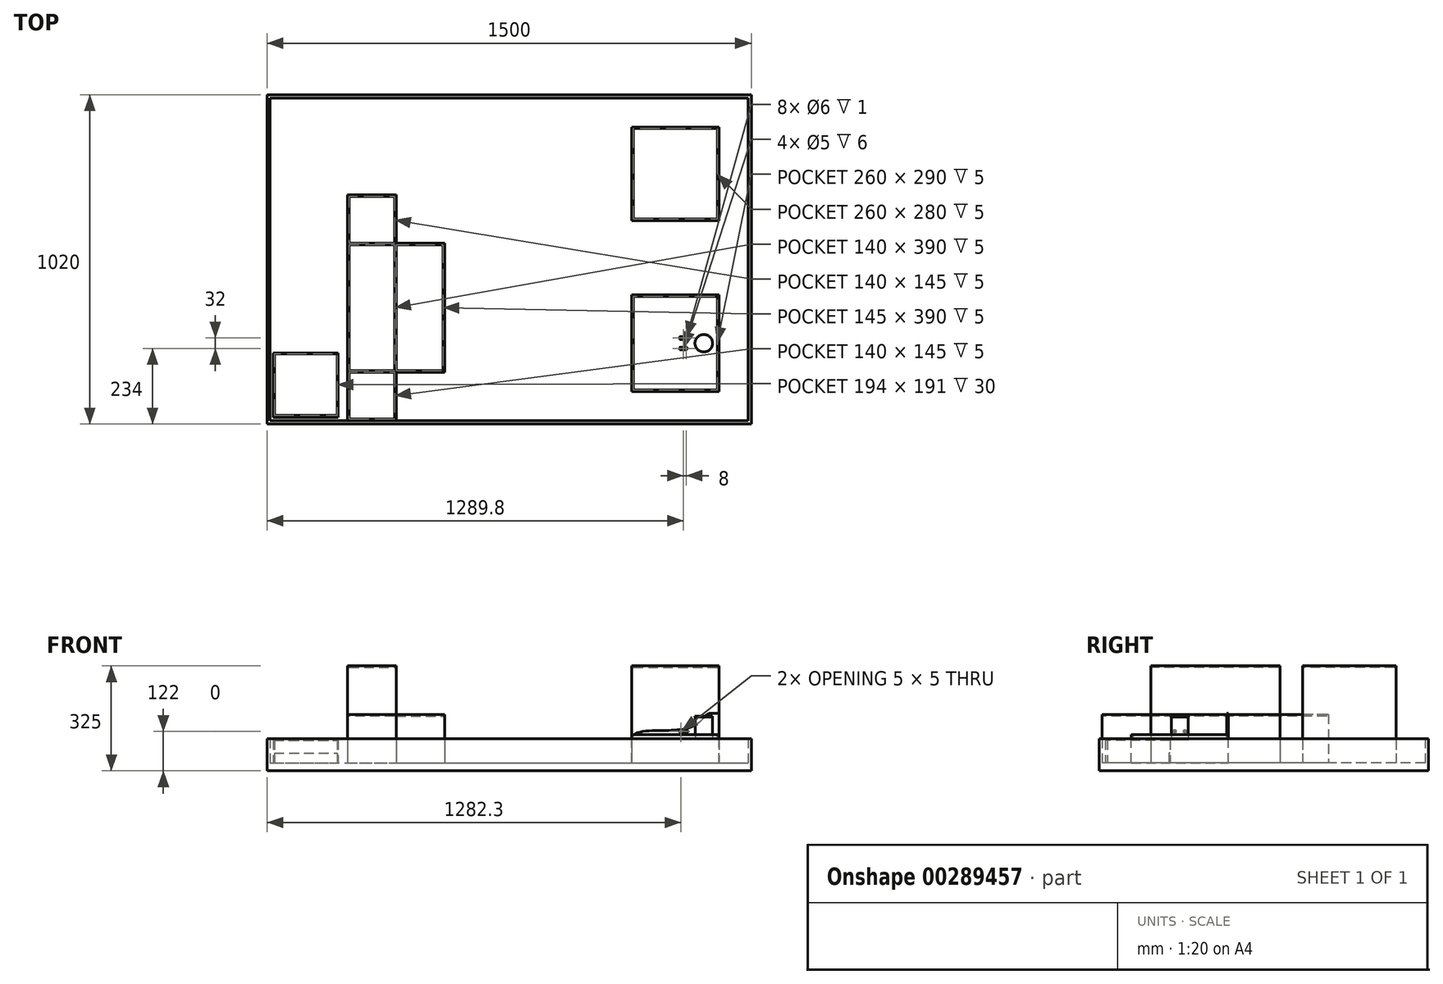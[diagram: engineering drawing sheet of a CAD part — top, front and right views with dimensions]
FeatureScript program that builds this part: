
annotation { "Feature Type Name" : "Feature", "Feature Type Description" : "" }
export const myFeature = defineFeature(function(context is Context, id is Id, definition is map)
    precondition{}
    {
        {
            var Q0;
            Q0=qCreatedBy(makeId("Top.planeOp"),FACE);
            var sketch = newSketch(context, id + "F0", { "sketchPlane" : qUnion([Q0])});
            skCircle(sketch, "E0", {"center": v(0, 0) * mm, "radius": 27.2 * mm});
            skSolve(sketch);
        }
        {
            var Q0;
            Q0 = qSketchRegion(id + "F0", true);
            extrude(context, id + "F1", {"entities" : qUnion([Q0]), "depth" : 2.83 * mm});
        }
        {
            var Q0;
            Q0=makeQuery(id+"F1.opExtrude","CAP_FACE",FACE,{"disambiguationData":[OSD([sQuery(id+"F0.wireOp",EDGE,"E0")])],"isStart":false});
            var sketch = newSketch(context, id + "F2", { "sketchPlane" : qUnion([Q0])});
            skCircle(sketch, "E1", {"center": v(0, 0) * mm, "radius": 26.4 * mm});
            skSolve(sketch);
        }
        {
            var Q0;
            Q0 = qSketchRegion(id + "F2", true);
            extrude(context, id + "F3", {"entities" : qUnion([Q0]), "operationType" : NewBodyOperationType.ADD, "depth" : 67.36 * mm});
        }
        {
            var Q0;
            Q0=makeQuery(id+"F3.opExtrude","CAP_FACE",FACE,{"disambiguationData":[OSD([sQuery(id+"F2.wireOp",EDGE,"E1")])],"isStart":false});
            var sketch = newSketch(context, id + "F4", { "sketchPlane" : qUnion([Q0])});
            skCircle(sketch, "E2", {"center": v(0, 0) * mm, "radius": 27.2 * mm});
            skSolve(sketch);
        }
        {
            var Q0;
            Q0 = qSketchRegion(id + "F4", true);
            extrude(context, id + "F5", {"entities" : qUnion([Q0]), "operationType" : NewBodyOperationType.ADD, "depth" : 2.83 * mm});
        }
        {
            var Q0;
            Q0=makeQuery(id+"F5.opExtrude","CAP_FACE",FACE,{"disambiguationData":[OSD([sQuery(id+"F4.wireOp",EDGE,"E2")])],"isStart":false});
            var sketch = newSketch(context, id + "F6", { "sketchPlane" : qUnion([Q0])});
            skSolve(sketch);
        }
        {
            var Q0;
            Q0=qCreatedBy(makeId("Top.planeOp"),FACE);
            cPlane(context, id + "F7", {"entities" : qUnion([Q0]), "cplaneType" : CPlaneType.OFFSET, "offset" : 25 * mm, "width" : 150 * mm, "height" : 150 * mm});
        }
        {
            var Q0;
            Q0=makeQuery(id+"F6.imprint","IMPRINT",FACE,{"disambiguationData":[TD([[makeQuery(id+"F6.imprint","IMPRINT",EDGE,{"derivedFrom":makeQuery(id+"F5.opExtrude","CAP_EDGE",EDGE,{"disambiguationData":[OSD([sQuery(id+"F4.wireOp",EDGE,"E2")])],"isStart":false})}),1.0]])]});
            var sketch = newSketch(context, id + "F8", { "sketchPlane" : qUnion([Q0])});
            skSolve(sketch);
        }
        {
            var Q0;
            Q0=qCreatedBy(makeId("Top.planeOp"),FACE);
            var sketch = newSketch(context, id + "F9", { "sketchPlane" : qUnion([Q0])});
            skLineSegment(sketch, "E3.bottom", {"start": v(-222.8, -150) * mm, "end": v(47.2, -150) * mm});
            skLineSegment(sketch, "E3.top", {"start": v(-222.8, 150) * mm, "end": v(47.2, 150) * mm});
            skLineSegment(sketch, "E3.left", {"start": v(-222.8, -150) * mm, "end": v(-222.8, 150) * mm});
            skLineSegment(sketch, "E3.right", {"start": v(47.2, -150) * mm, "end": v(47.2, 150) * mm});
            skSolve(sketch);
        }
        {
            var Q0;
            Q0 = qSketchRegion(id + "F9", true);
            extrude(context, id + "F10", {"entities" : qUnion([Q0]), "oppositeDirection" : true, "depth" : 72 * mm});
        }
        {
            var Q0;
            Q0=makeQuery(id+"F10.opExtrude","CAP_FACE",FACE,{"disambiguationData":[OSD([sQuery(id+"F9.wireOp",EDGE,"E3.bottom"),sQuery(id+"F9.wireOp",EDGE,"E3.top"),sQuery(id+"F9.wireOp",EDGE,"E3.left"),sQuery(id+"F9.wireOp",EDGE,"E3.right")])],"isStart":true});
            var sketch = newSketch(context, id + "F11", { "sketchPlane" : qUnion([Q0])});
            skLineSegment(sketch, "E4.bottom", {"start": v(-222.8, -150) * mm, "end": v(47.2, -150) * mm});
            skLineSegment(sketch, "E4.top", {"start": v(-222.8, -145) * mm, "end": v(42.2, -145) * mm});
            skLineSegment(sketch, "E4.left", {"start": v(-222.8, -150) * mm, "end": v(-222.8, -145) * mm});
            skLineSegment(sketch, "E5.bottom", {"start": v(47.2, 150) * mm, "end": v(42.2, 150) * mm});
            skLineSegment(sketch, "E5.left", {"start": v(47.2, 150) * mm, "end": v(47.2, -150) * mm});
            skLineSegment(sketch, "E5.right", {"start": v(42.2, 150) * mm, "end": v(42.2, -145) * mm});
            skSolve(sketch);
        }
        {
            var Q0;
            Q0 = qSketchRegion(id + "F11", true);
            extrude(context, id + "F12", {"entities" : qUnion([Q0]), "operationType" : NewBodyOperationType.ADD, "depth" : 15 * mm});
        }
        {
            var Q0;
            Q0=makeQuery(id+"F12.boolean.opBoolean","MERGE",FACE,{"derivedFrom":[makeQuery(id+"F10.opExtrude","SWEPT_FACE",FACE,{"disambiguationData":[OSD([sQuery(id+"F9.wireOp",EDGE,"E3.top")])]}),makeQuery(id+"F12.opExtrude","SWEPT_FACE",FACE,{"disambiguationData":[OSD([sQuery(id+"F11.wireOp",EDGE,"E5.bottom")])]})]});
            var sketch = newSketch(context, id + "F13", { "sketchPlane" : qUnion([Q0])});
            skLineSegment(sketch, "E6", {"start": v(-47.2, 81.36) * mm, "end": v(-21.31, 81.36) * mm});
            skFitSpline(sketch, "E7", {"points": [v(-21.31, 81.36) * mm, v(15.24, 52.01) * mm, v(114.14, 28.17) * mm, v(222.8, 0) * mm], "startDerivative": vector(181.02, 0.3) * mm, "endDerivative": vector(-1.73, -239.85) * mm});
            skLineSegment(sketch, "E8", {"start": v(-47.2, 81.36) * mm, "end": v(-47.2, -72) * mm});
            skLineSegment(sketch, "E9", {"start": v(-47.2, -72) * mm, "end": v(222.8, -72) * mm});
            skLineSegment(sketch, "E10", {"start": v(222.8, -72) * mm, "end": v(222.8, 0) * mm});
            skSolve(sketch);
        }
        {
            var Q0;
            Q0 = qSketchRegion(id + "F13", true);
            extrude(context, id + "F14", {"entities" : qUnion([Q0]), "operationType" : NewBodyOperationType.ADD, "oppositeDirection" : true, "depth" : 5 * mm});
        }
        {
            var Q0;
            Q0=makeQuery(id+"F10.opExtrude","CAP_FACE",FACE,{"disambiguationData":[OSD([sQuery(id+"F9.wireOp",EDGE,"E3.bottom"),sQuery(id+"F9.wireOp",EDGE,"E3.top"),sQuery(id+"F9.wireOp",EDGE,"E3.left"),sQuery(id+"F9.wireOp",EDGE,"E3.right")])],"isStart":true});
            var sketch = newSketch(context, id + "F15", { "sketchPlane" : qUnion([Q0])});
            skLineSegment(sketch, "E11.bottom", {"start": v(-222.8, 145) * mm, "end": v(-217.8, 145) * mm});
            skLineSegment(sketch, "E11.top", {"start": v(-222.8, -145) * mm, "end": v(-217.8, -145) * mm});
            skLineSegment(sketch, "E11.left", {"start": v(-222.8, 145) * mm, "end": v(-222.8, -145) * mm});
            skLineSegment(sketch, "E11.right", {"start": v(-217.8, 145) * mm, "end": v(-217.8, -145) * mm});
            skSolve(sketch);
        }
        {
            var Q0;
            Q0 = qSketchRegion(id + "F15", true);
            extrude(context, id + "F16", {"entities" : qUnion([Q0]), "operationType" : NewBodyOperationType.ADD, "depth" : 5 * mm});
        }
        {
            var Q0;
            Q0=makeQuery(id+"F10.opExtrude","CAP_FACE",FACE,{"disambiguationData":[OSD([sQuery(id+"F9.wireOp",EDGE,"E3.bottom"),sQuery(id+"F9.wireOp",EDGE,"E3.top"),sQuery(id+"F9.wireOp",EDGE,"E3.left"),sQuery(id+"F9.wireOp",EDGE,"E3.right")])],"isStart":false});
            var sketch = newSketch(context, id + "F17", { "sketchPlane" : qUnion([Q0])});
            skLineSegment(sketch, "E12.bottom", {"start": v(147.2, 250) * mm, "end": v(-1352.8, 250) * mm});
            skLineSegment(sketch, "E12.top", {"start": v(147.2, -770) * mm, "end": v(-1352.8, -770) * mm});
            skLineSegment(sketch, "E12.left", {"start": v(147.2, 250) * mm, "end": v(147.2, -770) * mm});
            skLineSegment(sketch, "E12.right", {"start": v(-1352.8, 250) * mm, "end": v(-1352.8, -770) * mm});
            skSolve(sketch);
        }
        {
            var Q0;
            Q0 = qSketchRegion(id + "F17", true);
            extrude(context, id + "F18", {"entities" : qUnion([Q0]), "operationType" : NewBodyOperationType.ADD, "depth" : 25 * mm});
        }
        {
            var Q0;
            Q0=makeQuery(id+"F18.opExtrude","CAP_FACE",FACE,{"disambiguationData":[OSD([sQuery(id+"F17.wireOp",EDGE,"E12.bottom"),sQuery(id+"F17.wireOp",EDGE,"E12.top"),sQuery(id+"F17.wireOp",EDGE,"E12.left"),sQuery(id+"F17.wireOp",EDGE,"E12.right")])],"isStart":true});
            var sketch = newSketch(context, id + "F19", { "sketchPlane" : qUnion([Q0])});
            skLineSegment(sketch, "E13.bottom", {"start": v(-222.8, 670) * mm, "end": v(47.2, 670) * mm});
            skLineSegment(sketch, "E13.top", {"start": v(-222.8, 380) * mm, "end": v(47.2, 380) * mm});
            skLineSegment(sketch, "E13.left", {"start": v(-222.8, 670) * mm, "end": v(-222.8, 380) * mm});
            skLineSegment(sketch, "E13.right", {"start": v(47.2, 670) * mm, "end": v(47.2, 380) * mm});
            skSolve(sketch);
        }
        {
            var Q0;
            Q0 = qSketchRegion(id + "F19", true);
            extrude(context, id + "F20", {"entities" : qUnion([Q0]), "operationType" : NewBodyOperationType.ADD, "depth" : 300 * mm});
        }
        {
            var Q0;
            Q0=makeQuery(id+"F20.opExtrude","CAP_FACE",FACE,{"disambiguationData":[OSD([sQuery(id+"F19.wireOp",EDGE,"E13.bottom"),sQuery(id+"F19.wireOp",EDGE,"E13.top"),sQuery(id+"F19.wireOp",EDGE,"E13.left"),sQuery(id+"F19.wireOp",EDGE,"E13.right")])],"isStart":false});
            var sketch = newSketch(context, id + "F21", { "sketchPlane" : qUnion([Q0])});
            skLineSegment(sketch, "E14.bottom", {"start": v(-217.8, 665) * mm, "end": v(42.2, 665) * mm});
            skLineSegment(sketch, "E14.top", {"start": v(-217.8, 385) * mm, "end": v(42.2, 385) * mm});
            skLineSegment(sketch, "E14.left", {"start": v(-217.8, 665) * mm, "end": v(-217.8, 385) * mm});
            skLineSegment(sketch, "E14.right", {"start": v(42.2, 665) * mm, "end": v(42.2, 385) * mm});
            skSolve(sketch);
        }
        {
            var Q0;
            Q0 = qSketchRegion(id + "F21", true);
            extrude(context, id + "F22", {"entities" : qUnion([Q0]), "operationType" : NewBodyOperationType.REMOVE, "oppositeDirection" : true, "depth" : 5 * mm});
        }
        {
            var Q0;
            Q0=makeQuery(id+"F18.opExtrude","CAP_FACE",FACE,{"disambiguationData":[OSD([sQuery(id+"F17.wireOp",EDGE,"E12.bottom"),sQuery(id+"F17.wireOp",EDGE,"E12.top"),sQuery(id+"F17.wireOp",EDGE,"E12.left"),sQuery(id+"F17.wireOp",EDGE,"E12.right")])],"isStart":true});
            var sketch = newSketch(context, id + "F23", { "sketchPlane" : qUnion([Q0])});
            skLineSegment(sketch, "E15.bottom", {"start": v(-1352.8, 770) * mm, "end": v(147.2, 770) * mm});
            skLineSegment(sketch, "E15.top", {"start": v(-1352.8, -250) * mm, "end": v(147.2, -250) * mm});
            skLineSegment(sketch, "E15.left", {"start": v(-1352.8, 770) * mm, "end": v(-1352.8, -250) * mm});
            skLineSegment(sketch, "E15.right", {"start": v(147.2, 770) * mm, "end": v(147.2, -250) * mm});
            skLineSegment(sketch, "E16.bottom", {"start": v(-1342.8, 760) * mm, "end": v(137.2, 760) * mm});
            skLineSegment(sketch, "E16.top", {"start": v(-1342.8, -240) * mm, "end": v(137.2, -240) * mm});
            skLineSegment(sketch, "E16.left", {"start": v(-1342.8, 760) * mm, "end": v(-1342.8, -240) * mm});
            skLineSegment(sketch, "E16.right", {"start": v(137.2, 760) * mm, "end": v(137.2, -240) * mm});
            skSolve(sketch);
        }
        {
            var Q0;
            Q0 = qSketchRegion(id + "F23", true);
            extrude(context, id + "F24", {"entities" : qUnion([Q0]), "operationType" : NewBodyOperationType.ADD, "depth" : 75 * mm});
        }
        {
            var Q0;
            Q0=makeQuery(id+"F18.opExtrude","CAP_FACE",FACE,{"disambiguationData":[OSD([sQuery(id+"F17.wireOp",EDGE,"E12.bottom"),sQuery(id+"F17.wireOp",EDGE,"E12.top"),sQuery(id+"F17.wireOp",EDGE,"E12.left"),sQuery(id+"F17.wireOp",EDGE,"E12.right")])],"isStart":true});
            var sketch = newSketch(context, id + "F25", { "sketchPlane" : qUnion([Q0])});
            skLineSegment(sketch, "E17.bottom", {"start": v(-1102.8, 460) * mm, "end": v(-952.8, 460) * mm});
            skLineSegment(sketch, "E17.top", {"start": v(-1102.8, -240) * mm, "end": v(-952.8, -240) * mm});
            skLineSegment(sketch, "E17.left", {"start": v(-1102.8, 460) * mm, "end": v(-1102.8, -240) * mm});
            skLineSegment(sketch, "E17.right", {"start": v(-952.8, 460) * mm, "end": v(-952.8, 310) * mm});
            skLineSegment(sketch, "E18.bottom", {"start": v(-952.8, 310) * mm, "end": v(-802.8, 310) * mm});
            skLineSegment(sketch, "E18.top", {"start": v(-952.8, -90) * mm, "end": v(-802.8, -90) * mm});
            skLineSegment(sketch, "E18.right", {"start": v(-802.8, 310) * mm, "end": v(-802.8, -90) * mm});
            skLineSegment(sketch, "E19.trimOffspring", {"start": v(-952.8, -90) * mm, "end": v(-952.8, -240) * mm});
            skSolve(sketch);
        }
        {
            var Q0;
            Q0 = qSketchRegion(id + "F25", true);
            extrude(context, id + "F26", {"entities" : qUnion([Q0]), "operationType" : NewBodyOperationType.ADD, "depth" : 150 * mm});
        }
        {
            var Q0;
            Q0=makeQuery(id+"F26.opExtrude","CAP_FACE",FACE,{"disambiguationData":[OSD([sQuery(id+"F25.wireOp",EDGE,"E17.bottom"),sQuery(id+"F25.wireOp",EDGE,"E17.top"),sQuery(id+"F25.wireOp",EDGE,"E17.left"),sQuery(id+"F25.wireOp",EDGE,"E17.right"),sQuery(id+"F25.wireOp",EDGE,"E18.bottom"),sQuery(id+"F25.wireOp",EDGE,"E18.top"),sQuery(id+"F25.wireOp",EDGE,"E18.right"),sQuery(id+"F25.wireOp",EDGE,"E19.trimOffspring")])],"isStart":false});
            var sketch = newSketch(context, id + "F27", { "sketchPlane" : qUnion([Q0])});
            skLineSegment(sketch, "E20.bottom", {"start": v(-952.8, 310) * mm, "end": v(-1102.8, 310) * mm});
            skLineSegment(sketch, "E20.top", {"start": v(-952.8, -90) * mm, "end": v(-1102.8, -90) * mm});
            skLineSegment(sketch, "E20.left", {"start": v(-952.8, 310) * mm, "end": v(-952.8, -90) * mm});
            skLineSegment(sketch, "E20.right", {"start": v(-1102.8, 310) * mm, "end": v(-1102.8, -90) * mm});
            skSolve(sketch);
        }
        {
            var Q0;
            Q0 = qSketchRegion(id + "F27", true);
            extrude(context, id + "F28", {"entities" : qUnion([Q0]), "operationType" : NewBodyOperationType.ADD, "depth" : 150 * mm});
        }
        {
            var Q0;
            Q0=makeQuery(id+"F28.opExtrude","CAP_FACE",FACE,{"disambiguationData":[OSD([sQuery(id+"F27.wireOp",EDGE,"E20.bottom"),sQuery(id+"F27.wireOp",EDGE,"E20.top"),sQuery(id+"F27.wireOp",EDGE,"E20.left"),sQuery(id+"F27.wireOp",EDGE,"E20.right")])],"isStart":false});
            var sketch = newSketch(context, id + "F29", { "sketchPlane" : qUnion([Q0])});
            skLineSegment(sketch, "E21.bottom", {"start": v(-1097.8, 305) * mm, "end": v(-957.8, 305) * mm});
            skLineSegment(sketch, "E21.top", {"start": v(-1097.8, -85) * mm, "end": v(-957.8, -85) * mm});
            skLineSegment(sketch, "E21.left", {"start": v(-1097.8, 305) * mm, "end": v(-1097.8, -85) * mm});
            skLineSegment(sketch, "E21.right", {"start": v(-957.8, 305) * mm, "end": v(-957.8, -85) * mm});
            skSolve(sketch);
        }
        {
            var Q0;
            Q0 = qSketchRegion(id + "F29", true);
            extrude(context, id + "F30", {"entities" : qUnion([Q0]), "operationType" : NewBodyOperationType.REMOVE, "oppositeDirection" : true, "depth" : 5 * mm});
        }
        {
            var Q0;
            {var subQ0=sQuery(id+"F25.wireOp",EDGE,"E17.left");var subQ1=sQuery(id+"F25.wireOp",EDGE,"E18.bottom");var subQ2=sQuery(id+"F25.wireOp",EDGE,"E17.right");var subQ3=sQuery(id+"F25.wireOp",EDGE,"E17.bottom");var subQ4=makeQuery(id+"F26.opExtrude","CAP_FACE",FACE,{"disambiguationData":[OSD([subQ3,sQuery(id+"F25.wireOp",EDGE,"E17.top"),subQ0,subQ2,subQ1,sQuery(id+"F25.wireOp",EDGE,"E18.top"),sQuery(id+"F25.wireOp",EDGE,"E18.right"),sQuery(id+"F25.wireOp",EDGE,"E19.trimOffspring")])],"isStart":false});Q0=makeQuery(id+"F28.boolean.opBoolean","SPLIT",FACE,{"disambiguationData":[TD([makeQuery(id+"F26.opExtrude","SWEPT_FACE",FACE,{"disambiguationData":[OSD([subQ3])]})])],"derivedFrom":subQ4});}
            var sketch = newSketch(context, id + "F31", { "sketchPlane" : qUnion([Q0])});
            skLineSegment(sketch, "E22.bottom", {"start": v(-1097.8, 455) * mm, "end": v(-957.8, 455) * mm});
            skLineSegment(sketch, "E22.top", {"start": v(-1097.8, 310) * mm, "end": v(-957.8, 310) * mm});
            skLineSegment(sketch, "E22.left", {"start": v(-1097.8, 455) * mm, "end": v(-1097.8, 310) * mm});
            skLineSegment(sketch, "E22.right", {"start": v(-957.8, 455) * mm, "end": v(-957.8, 310) * mm});
            skLineSegment(sketch, "E23.bottom", {"start": v(-952.8, 305) * mm, "end": v(-807.8, 305) * mm});
            skLineSegment(sketch, "E23.top", {"start": v(-952.8, -85) * mm, "end": v(-807.8, -85) * mm});
            skLineSegment(sketch, "E23.left", {"start": v(-952.8, 305) * mm, "end": v(-952.8, -85) * mm});
            skLineSegment(sketch, "E23.right", {"start": v(-807.8, 305) * mm, "end": v(-807.8, -85) * mm});
            skLineSegment(sketch, "E24.bottom", {"start": v(-1097.8, -90) * mm, "end": v(-957.8, -90) * mm});
            skLineSegment(sketch, "E24.top", {"start": v(-1097.8, -235) * mm, "end": v(-957.8, -235) * mm});
            skLineSegment(sketch, "E24.left", {"start": v(-1097.8, -90) * mm, "end": v(-1097.8, -235) * mm});
            skLineSegment(sketch, "E24.right", {"start": v(-957.8, -90) * mm, "end": v(-957.8, -235) * mm});
            skSolve(sketch);
        }
        {
            var Q0;
            Q0 = qSketchRegion(id + "F31", true);
            extrude(context, id + "F32", {"entities" : qUnion([Q0]), "operationType" : NewBodyOperationType.REMOVE, "oppositeDirection" : true, "depth" : 5 * mm});
        }
        {
            var Q0;
            Q0=qCreatedBy(id+"F7.planeOp",FACE);
            var sketch = newSketch(context, id + "F33", { "sketchPlane" : qUnion([Q0])});
            skLineSegment(sketch, "E25", {"start": v(0, 0) * mm, "end": v(-90, 0) * mm, "construction": true});
            skLineSegment(sketch, "E26.bottom", {"start": v(-74.5, -12) * mm, "end": v(-55, -12) * mm});
            skLineSegment(sketch, "E26.top", {"start": v(-74.5, -20) * mm, "end": v(-55, -20) * mm});
            skLineSegment(sketch, "E26.left", {"start": v(-74.5, -12) * mm, "end": v(-74.5, -13) * mm});
            skPoint(sketch, "E27.visualSharp", {"position": v(-51, -12) * mm});
            skPoint(sketch, "E28.visualSharp", {"position": v(-51, -20) * mm});
            skCircle(sketch, "E29", {"center": v(-55, -16) * mm, "radius": 3 * mm});
            skLineSegment(sketch, "E30", {"start": v(-59, -3.98) * mm, "end": v(-59, -18.08) * mm, "construction": true});
            skCircle(sketch, "E31.MirrorC", {"center": v(-63, -16) * mm, "radius": 3 * mm});
            skLineSegment(sketch, "E32.bottom", {"start": v(-74.5, -13) * mm, "end": v(-65.65, -13) * mm});
            skLineSegment(sketch, "E32.top", {"start": v(-74.5, -19) * mm, "end": v(-65.65, -19) * mm});
            skArc(sketch, "E33", {"start": v(-65.65, -13) * mm, "mid": v(-67, -16) * mm, "end": v(-65.65, -19) * mm});
            skLineSegment(sketch, "E34.trimOffspring", {"start": v(-74.5, -19) * mm, "end": v(-74.5, -20) * mm});
            skArc(sketch, "E35.trimOffspring", {"start": v(-55, -20) * mm, "mid": v(-51, -16) * mm, "end": v(-55, -12) * mm});
            skLineSegment(sketch, "E36.MirrorCS", {"start": v(-74.5, 12) * mm, "end": v(-74.5, 13) * mm});
            skLineSegment(sketch, "E37.MirrorCS", {"start": v(-74.5, 19) * mm, "end": v(-74.5, 20) * mm});
            skPoint(sketch, "E38.MirrorP", {"position": v(-51, 12) * mm});
            skLineSegment(sketch, "E39.MirrorCS", {"start": v(-74.5, 12) * mm, "end": v(-55, 12) * mm});
            skPoint(sketch, "E40.MirrorP", {"position": v(-51, 20) * mm});
            skArc(sketch, "E41.MirrorCS", {"start": v(-65.65, 13) * mm, "mid": v(-67, 16) * mm, "end": v(-65.65, 19) * mm});
            skArc(sketch, "E42.MirrorCS", {"start": v(-55, 20) * mm, "mid": v(-51, 16) * mm, "end": v(-55, 12) * mm});
            skLineSegment(sketch, "E43.MirrorCS", {"start": v(-74.5, 20) * mm, "end": v(-55, 20) * mm});
            skCircle(sketch, "E44.MirrorC", {"center": v(-55, 16) * mm, "radius": 3 * mm});
            skCircle(sketch, "E45.MirrorC", {"center": v(-63, 16) * mm, "radius": 3 * mm});
            skLineSegment(sketch, "E46.MirrorCS", {"start": v(-74.5, 19) * mm, "end": v(-65.65, 19) * mm});
            skLineSegment(sketch, "E47.MirrorCS", {"start": v(-74.5, 13) * mm, "end": v(-65.65, 13) * mm});
            skSolve(sketch);
        }
        {
            var Q0;
            Q0 = qSketchRegion(id + "F33", true);
            var Q1;
            Q1 = qSketchRegion(id + "F36", true);
            extrude(context, id + "F34", {"entities" : qUnion([Q0, Q1]), "endBound" : BoundingType.SYMMETRIC, "depth" : 8 * mm});
        }
        {
            var Q0;
            Q0=makeQuery(id+"F34.opExtrude","CAP_EDGE",EDGE,{"disambiguationData":[OSD([sQuery(id+"F33.wireOp",EDGE,"E34.trimOffspring")])],"isStart":false});
            var Q1;
            Q1=makeQuery(id+"F34.opExtrude","CAP_EDGE",EDGE,{"disambiguationData":[OSD([sQuery(id+"F33.wireOp",EDGE,"E26.left")])],"isStart":false});
            var Q2;
            Q2=makeQuery(id+"F34.opExtrude","CAP_EDGE",EDGE,{"disambiguationData":[OSD([sQuery(id+"F33.wireOp",EDGE,"E34.trimOffspring")])],"isStart":true});
            var Q3;
            Q3=makeQuery(id+"F34.opExtrude","CAP_EDGE",EDGE,{"disambiguationData":[OSD([sQuery(id+"F33.wireOp",EDGE,"E26.left")])],"isStart":true});
            var Q4;
            Q4=makeQuery(id+"F34.opExtrude","CAP_EDGE",EDGE,{"disambiguationData":[OSD([sQuery(id+"F33.wireOp",EDGE,"E36.MirrorCS")])],"isStart":false});
            var Q5;
            Q5=makeQuery(id+"F34.opExtrude","CAP_EDGE",EDGE,{"disambiguationData":[OSD([sQuery(id+"F33.wireOp",EDGE,"E37.MirrorCS")])],"isStart":false});
            var Q6;
            Q6=makeQuery(id+"F34.opExtrude","CAP_EDGE",EDGE,{"disambiguationData":[OSD([sQuery(id+"F33.wireOp",EDGE,"E37.MirrorCS")])],"isStart":true});
            var Q7;
            Q7=makeQuery(id+"F34.opExtrude","CAP_EDGE",EDGE,{"disambiguationData":[OSD([sQuery(id+"F33.wireOp",EDGE,"E36.MirrorCS")])],"isStart":true});
            fillet(context, id + "F35", {"entities" : qUnion([Q0, Q1, Q2, Q3, Q4, Q5, Q6, Q7]), "radius" : 4 * mm, "tangentPropagation" : true, "allowEdgeOverflow" : false});
        }
        {
            var Q0;
            Q0=makeQuery(id+"F34.opExtrude","SWEPT_FACE",FACE,{"disambiguationData":[OSD([sQuery(id+"F33.wireOp",EDGE,"E26.top")])]});
            var sketch = newSketch(context, id + "F36", { "sketchPlane" : qUnion([Q0])});
            skCircle(sketch, "E48", {"center": v(-70.5, 25) * mm, "radius": 3 * mm});
            skSolve(sketch);
        }
        {
            var Q0;
            Q0 = qSketchRegion(id + "F36", true);
            var Q1;
            Q1=makeQuery(id+"F34.opExtrude","SWEPT_FACE",FACE,{"disambiguationData":[OSD([sQuery(id+"F33.wireOp",EDGE,"E26.bottom")])]});
            extrude(context, id + "F37", {"entities" : qUnion([Q0]), "operationType" : NewBodyOperationType.ADD, "endBound" : BoundingType.UP_TO_SURFACE, "oppositeDirection" : true, "endBoundEntityFace" : qUnion([Q1]), "depth" : 25 * mm});
        }
        {
            var Q0;
            Q0=makeQuery(id+"F34.opExtrude","SWEPT_FACE",FACE,{"disambiguationData":[OSD([sQuery(id+"F33.wireOp",EDGE,"E43.MirrorCS")])]});
            var sketch = newSketch(context, id + "F38", { "sketchPlane" : qUnion([Q0])});
            skCircle(sketch, "E49", {"center": v(70.5, 25) * mm, "radius": 3 * mm});
            skSolve(sketch);
        }
        {
            var Q0;
            Q0 = qSketchRegion(id + "F38", true);
            var Q1;
            Q1=makeQuery(id+"F34.opExtrude","SWEPT_FACE",FACE,{"disambiguationData":[OSD([sQuery(id+"F33.wireOp",EDGE,"E39.MirrorCS")])]});
            extrude(context, id + "F39", {"entities" : qUnion([Q0]), "operationType" : NewBodyOperationType.ADD, "endBound" : BoundingType.UP_TO_SURFACE, "oppositeDirection" : true, "endBoundEntityFace" : qUnion([Q1]), "depth" : 25 * mm});
        }
        {
            var Q0;
            Q0=qCreatedBy(id+"F7.planeOp",FACE);
            var sketch = newSketch(context, id + "F40", { "sketchPlane" : qUnion([Q0])});
            skCircle(sketch, "E50", {"center": v(-55, 16) * mm, "radius": 3 * mm});
            skCircle(sketch, "E51", {"center": v(-63, 16) * mm, "radius": 2.5 * mm});
            skCircle(sketch, "E52", {"center": v(-63, 16) * mm, "radius": 3 * mm});
            skCircle(sketch, "E53", {"center": v(-55, 16) * mm, "radius": 2.5 * mm});
            skSolve(sketch);
        }
        {
            var Q0;
            Q0 = qSketchRegion(id + "F40", true);
            extrude(context, id + "F41", {"entities" : qUnion([Q0]), "operationType" : NewBodyOperationType.ADD, "endBound" : BoundingType.SYMMETRIC, "depth" : 6 * mm});
        }
        {
            var Q0;
            Q0=qCreatedBy(id+"F7.planeOp",FACE);
            var sketch = newSketch(context, id + "F42", { "sketchPlane" : qUnion([Q0])});
            skCircle(sketch, "E54", {"center": v(-63, -16) * mm, "radius": 2.5 * mm});
            skCircle(sketch, "E55", {"center": v(-63, -16) * mm, "radius": 3 * mm});
            skCircle(sketch, "E56", {"center": v(-55, -16) * mm, "radius": 2.5 * mm});
            skCircle(sketch, "E57", {"center": v(-55, -16) * mm, "radius": 3 * mm});
            skSolve(sketch);
        }
        {
            var Q0;
            Q0 = qSketchRegion(id + "F42", true);
            extrude(context, id + "F43", {"entities" : qUnion([Q0]), "operationType" : NewBodyOperationType.ADD, "endBound" : BoundingType.SYMMETRIC, "depth" : 6 * mm});
        }
        {
            var Q0;
            Q0=makeQuery(id+"F34.opExtrude","SWEPT_FACE",FACE,{"disambiguationData":[OSD([sQuery(id+"F33.wireOp",EDGE,"E43.MirrorCS")])]});
            var sketch = newSketch(context, id + "F44", { "sketchPlane" : qUnion([Q0])});
            skArc(sketch, "E58", {"start": v(71.5, 27.3) * mm, "mid": v(70.5, 27.5) * mm, "end": v(69.5, 27.3) * mm});
            skLineSegment(sketch, "E59.bottom", {"start": v(68.2, 26) * mm, "end": v(69.5, 26) * mm});
            skLineSegment(sketch, "E59.top", {"start": v(68.2, 24) * mm, "end": v(69.5, 24) * mm});
            skLineSegment(sketch, "E60.left", {"start": v(71.5, 27.3) * mm, "end": v(71.5, 26) * mm});
            skLineSegment(sketch, "E60.right", {"start": v(69.5, 27.3) * mm, "end": v(69.5, 26) * mm});
            skPoint(sketch, "E61.orphan", {"position": v(69.5, 27.8) * mm});
            skPoint(sketch, "E62.orphan", {"position": v(71.5, 27.8) * mm});
            skArc(sketch, "E63.trimOffspring", {"start": v(68.2, 26) * mm, "mid": v(68, 25) * mm, "end": v(68.2, 24) * mm});
            skPoint(sketch, "E59.left.start.orphan", {"position": v(67.32, 26) * mm});
            skPoint(sketch, "E64.orphan", {"position": v(67.32, 24) * mm});
            skArc(sketch, "E65.trimOffspring", {"start": v(69.5, 22.7) * mm, "mid": v(70.5, 22.5) * mm, "end": v(71.5, 22.7) * mm});
            skLineSegment(sketch, "E66.trimOffspring", {"start": v(69.5, 24) * mm, "end": v(69.5, 22.7) * mm});
            skLineSegment(sketch, "E67.trimOffspring", {"start": v(71.5, 26) * mm, "end": v(72.8, 26) * mm});
            skLineSegment(sketch, "E68.trimOffspring", {"start": v(71.5, 24) * mm, "end": v(71.5, 22.7) * mm});
            skLineSegment(sketch, "E69.trimOffspring", {"start": v(71.5, 24) * mm, "end": v(72.8, 24) * mm});
            skPoint(sketch, "E60.top.end.orphan", {"position": v(69.5, 22.2) * mm});
            skPoint(sketch, "E70.orphan", {"position": v(71.5, 22.2) * mm});
            skPoint(sketch, "E59.right.end.orphan", {"position": v(73.68, 24) * mm});
            skPoint(sketch, "E71.orphan", {"position": v(73.68, 26) * mm});
            skArc(sketch, "E72.trimOffspring", {"start": v(72.8, 24) * mm, "mid": v(73, 25) * mm, "end": v(72.8, 26) * mm});
            skSolve(sketch);
        }
        {
            var Q0;
            Q0 = qSketchRegion(id + "F44", true);
            extrude(context, id + "F45", {"entities" : qUnion([Q0]), "operationType" : NewBodyOperationType.REMOVE, "endBound" : BoundingType.THROUGH_ALL, "oppositeDirection" : true, "depth" : 25 * mm});
        }
        {
            var Q0;
            Q0=makeQuery(id+"F18.opExtrude","CAP_FACE",FACE,{"disambiguationData":[OSD([sQuery(id+"F17.wireOp",EDGE,"E12.bottom"),sQuery(id+"F17.wireOp",EDGE,"E12.top"),sQuery(id+"F17.wireOp",EDGE,"E12.left"),sQuery(id+"F17.wireOp",EDGE,"E12.right")])],"isStart":true});
            var sketch = newSketch(context, id + "F46", { "sketchPlane" : qUnion([Q0])});
            skLineSegment(sketch, "E73.bottom", {"start": v(-1332.8, -30) * mm, "end": v(-1132.8, -30) * mm});
            skLineSegment(sketch, "E73.top", {"start": v(-1332.8, -230) * mm, "end": v(-1132.8, -230) * mm});
            skLineSegment(sketch, "E73.left", {"start": v(-1332.8, -30) * mm, "end": v(-1332.8, -230) * mm});
            skLineSegment(sketch, "E73.right", {"start": v(-1132.8, -30) * mm, "end": v(-1132.8, -230) * mm});
            skLineSegment(sketch, "E74.bottom", {"start": v(-1329.8, -33) * mm, "end": v(-1135.8, -33) * mm});
            skLineSegment(sketch, "E74.top", {"start": v(-1329.8, -224) * mm, "end": v(-1135.8, -224) * mm});
            skLineSegment(sketch, "E74.left", {"start": v(-1329.8, -33) * mm, "end": v(-1329.8, -224) * mm});
            skLineSegment(sketch, "E74.right", {"start": v(-1135.8, -33) * mm, "end": v(-1135.8, -224) * mm});
            skSolve(sketch);
        }
        {
            var Q0;
            Q0 = qSketchRegion(id + "F46", true);
            extrude(context, id + "F47", {"entities" : qUnion([Q0]), "operationType" : NewBodyOperationType.ADD, "depth" : 30 * mm});
        }
        {
            var Q0;
            Q0=makeQuery(id+"F47.opExtrude","CAP_FACE",FACE,{"disambiguationData":[OSD([sQuery(id+"F46.wireOp",EDGE,"E73.bottom"),sQuery(id+"F46.wireOp",EDGE,"E73.top"),sQuery(id+"F46.wireOp",EDGE,"E73.left"),sQuery(id+"F46.wireOp",EDGE,"E73.right"),sQuery(id+"F46.wireOp",EDGE,"E74.bottom"),sQuery(id+"F46.wireOp",EDGE,"E74.top"),sQuery(id+"F46.wireOp",EDGE,"E74.left"),sQuery(id+"F46.wireOp",EDGE,"E74.right")])],"isStart":false});
            var sketch = newSketch(context, id + "F48", { "sketchPlane" : qUnion([Q0])});
            skLineSegment(sketch, "E75.bottom", {"start": v(-1332.8, -30) * mm, "end": v(-1329.8, -30) * mm});
            skLineSegment(sketch, "E75.top", {"start": v(-1332.8, -230) * mm, "end": v(-1329.8, -230) * mm});
            skLineSegment(sketch, "E75.left", {"start": v(-1332.8, -30) * mm, "end": v(-1332.8, -230) * mm});
            skLineSegment(sketch, "E75.right", {"start": v(-1329.8, -30) * mm, "end": v(-1329.8, -224) * mm});
            skLineSegment(sketch, "E76.bottom", {"start": v(-1329.8, -230) * mm, "end": v(-1135.8, -230) * mm});
            skLineSegment(sketch, "E76.top", {"start": v(-1329.8, -224) * mm, "end": v(-1135.8, -224) * mm});
            skLineSegment(sketch, "E77.bottom", {"start": v(-1135.8, -230) * mm, "end": v(-1132.8, -230) * mm});
            skLineSegment(sketch, "E77.top", {"start": v(-1135.8, -30) * mm, "end": v(-1132.8, -30) * mm});
            skLineSegment(sketch, "E77.left", {"start": v(-1135.8, -224) * mm, "end": v(-1135.8, -30) * mm});
            skLineSegment(sketch, "E77.right", {"start": v(-1132.8, -230) * mm, "end": v(-1132.8, -30) * mm});
            skSolve(sketch);
        }
        {
            var Q0;
            Q0 = qSketchRegion(id + "F48", true);
            extrude(context, id + "F49", {"entities" : qUnion([Q0]), "operationType" : NewBodyOperationType.ADD, "depth" : 40 * mm});
        }
    });
